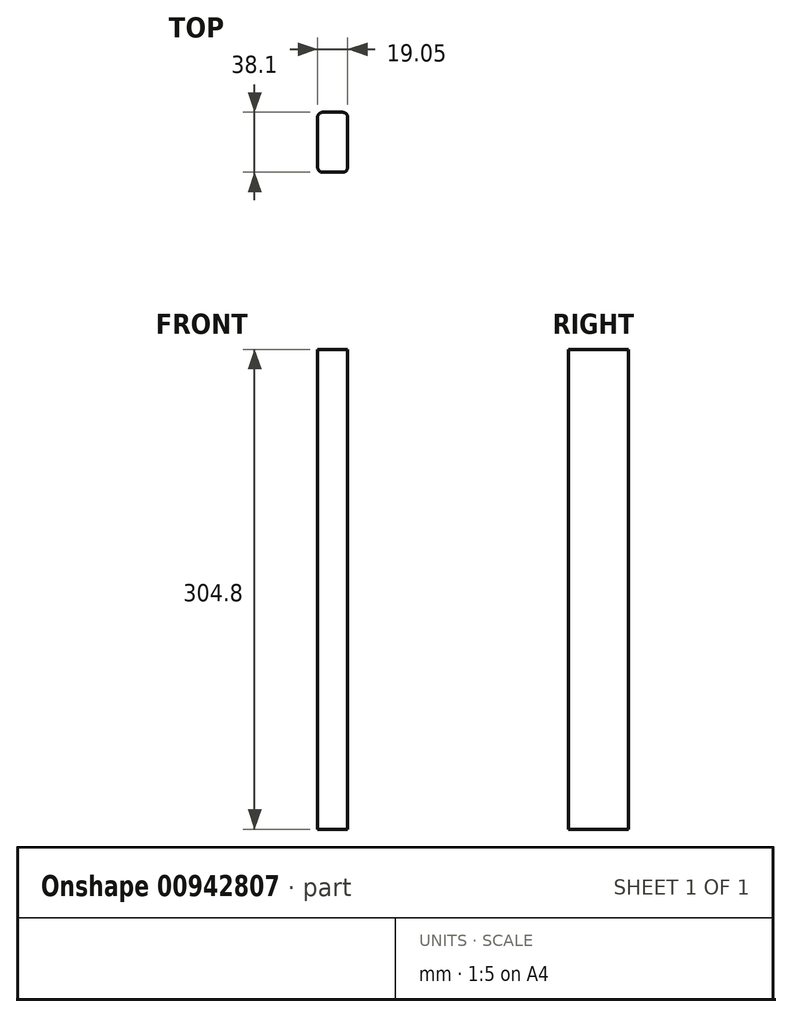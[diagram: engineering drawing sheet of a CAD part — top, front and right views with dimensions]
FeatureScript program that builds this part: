
annotation { "Feature Type Name" : "Feature", "Feature Type Description" : "" }
export const myFeature = defineFeature(function(context is Context, id is Id, definition is map)
    precondition{}
    {
        {
            var Q0;
            Q0=qCreatedBy(makeId("Top.planeOp"),FACE);
            var sketch = newSketch(context, id + "F0", { "sketchPlane" : qUnion([Q0])});
            skLineSegment(sketch, "E0.bottom", {"start": v(3.15, 0) * mm, "end": v(15.9, 0) * mm});
            skLineSegment(sketch, "E0.top", {"start": v(3.15, 38.1) * mm, "end": v(15.9, 38.1) * mm});
            skLineSegment(sketch, "E0.left", {"start": v(0, 3.15) * mm, "end": v(0, 34.95) * mm});
            skLineSegment(sketch, "E0.right", {"start": v(19.05, 3.15) * mm, "end": v(19.05, 34.95) * mm});
            skPoint(sketch, "E1.visualSharp", {"position": v(0, 38.1) * mm});
            skArc(sketch, "E1.filletArc", {"start": v(3.15, 38.1) * mm, "mid": v(0.92, 37.18) * mm, "end": v(0, 34.95) * mm});
            skArc(sketch, "E2.filletArc", {"start": v(19.05, 34.95) * mm, "mid": v(18.13, 37.18) * mm, "end": v(15.9, 38.1) * mm});
            skPoint(sketch, "E3.visualSharp", {"position": v(19.05, 0) * mm});
            skArc(sketch, "E3.filletArc", {"start": v(15.9, 0) * mm, "mid": v(18.13, 0.92) * mm, "end": v(19.05, 3.15) * mm});
            skPoint(sketch, "E4.visualSharp", {"position": v(0, 0) * mm});
            skArc(sketch, "E4.filletArc", {"start": v(0, 3.15) * mm, "mid": v(0.92, 0.92) * mm, "end": v(3.15, 0) * mm});
            skLineSegment(sketch, "E5.bottom", {"start": v(22.2, 0) * mm, "end": v(34.95, 0) * mm});
            skLineSegment(sketch, "E5.right", {"start": v(38.1, 3.15) * mm, "end": v(38.1, 34.95) * mm});
            skArc(sketch, "E6.filletArc", {"start": v(22.2, 38.1) * mm, "mid": v(19.97, 37.18) * mm, "end": v(19.05, 34.95) * mm});
            skArc(sketch, "E7.filletArc", {"start": v(38.1, 34.95) * mm, "mid": v(37.18, 37.18) * mm, "end": v(34.95, 38.1) * mm});
            skArc(sketch, "E8.filletArc", {"start": v(34.95, 0) * mm, "mid": v(37.18, 0.92) * mm, "end": v(38.1, 3.15) * mm});
            skArc(sketch, "E9.filletArc", {"start": v(19.05, 3.15) * mm, "mid": v(19.97, 0.92) * mm, "end": v(22.2, 0) * mm});
            skLineSegment(sketch, "E10", {"start": v(22.2, 38.1) * mm, "end": v(34.95, 38.1) * mm});
            skSolve(sketch);
        }
        {
            var Q0;
            Q0=makeQuery(id+"F0.imprint","IMPRINT",FACE,{"disambiguationData":[TD([[makeQuery(id+"F0.imprint","IMPRINT",EDGE,{"derivedFrom":sQuery(id+"F0.wireOp",EDGE,"E5.bottom")}),1.0]])]});
            var Q1;
            Q1=makeQuery(id+"F0.imprint","IMPRINT",FACE,{"disambiguationData":[TD([[makeQuery(id+"F0.imprint","IMPRINT",EDGE,{"derivedFrom":sQuery(id+"F0.wireOp",EDGE,"b7ff1907-7b2b-4cdd-8ea5-b45dade5522d.bottom")}),1.0]])]});
            var Q2;
            Q2=makeQuery(id+"F0.imprint","IMPRINT",FACE,{"disambiguationData":[TD([[makeQuery(id+"F0.imprint","IMPRINT",EDGE,{"derivedFrom":sQuery(id+"F0.wireOp",EDGE,"66c86851-db75-4c71-9093-7621e61d7ab7.bottom")}),1.0]])]});
            extrude(context, id + "F1", {"entities" : qUnion([Q0, Q1, Q2]), "depth" : 304.8 * mm, "offsetDistance" : 25.4 * mm});
        }
    });
